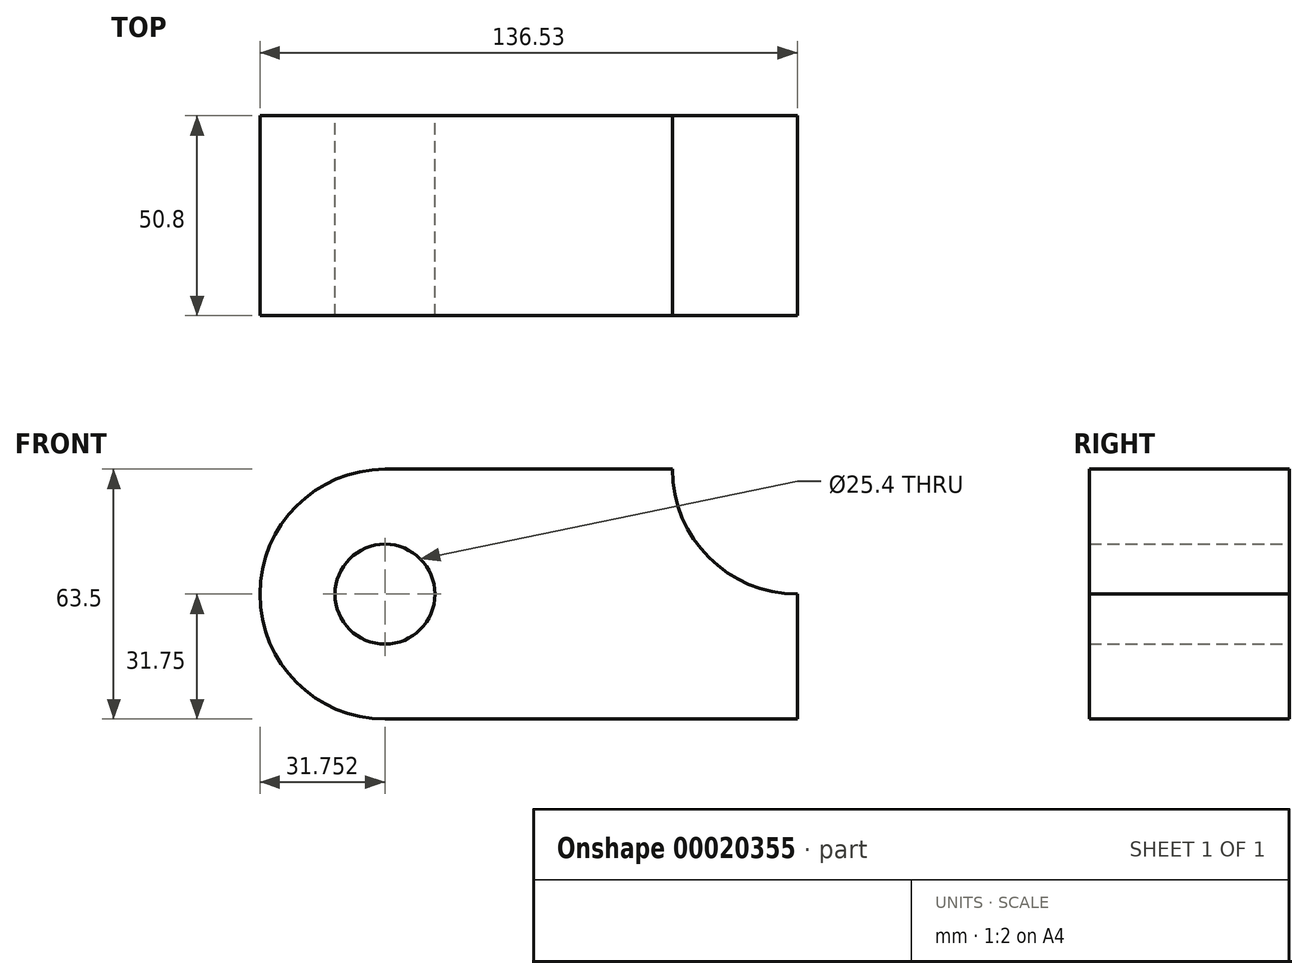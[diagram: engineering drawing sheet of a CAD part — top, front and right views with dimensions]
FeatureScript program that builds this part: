
annotation { "Feature Type Name" : "Feature", "Feature Type Description" : "" }
export const myFeature = defineFeature(function(context is Context, id is Id, definition is map)
    precondition{}
    {
        {
            var Q0;
            Q0=qCreatedBy(makeId("Front.planeOp"),FACE);
            var sketch = newSketch(context, id + "F0", { "sketchPlane" : qUnion([Q0])});
            skLineSegment(sketch, "E0.rect.bottom", {"start": v(-52.39, 31.75) * mm, "end": v(52.39, 31.75) * mm});
            skLineSegment(sketch, "E0.rect.top", {"start": v(-52.39, -31.75) * mm, "end": v(52.39, -31.75) * mm});
            skLineSegment(sketch, "E0.rect.left", {"start": v(-52.39, 31.75) * mm, "end": v(-52.39, -31.75) * mm});
            skLineSegment(sketch, "E0.rect.right", {"start": v(52.39, 31.75) * mm, "end": v(52.39, -31.75) * mm});
            skPoint(sketch, "E0.rect.middle", {"position": v(0, 0) * mm});
            skCircle(sketch, "E1", {"center": v(52.39, 31.75) * mm, "radius": 31.75 * mm});
            skCircle(sketch, "E2", {"center": v(-52.39, 0) * mm, "radius": 12.7 * mm});
            skCircle(sketch, "E3", {"center": v(-52.39, 0) * mm, "radius": 31.75 * mm});
            skSolve(sketch);
        }
        {
            var Q0;
            {var subQ1=sQuery(id+"F0.wireOp",EDGE,"E0.rect.top");Q0=makeQuery(id+"F0.imprint","IMPRINT",FACE,{"disambiguationData":[TD([[makeQuery(id+"F0.imprint","IMPRINT",EDGE,{"derivedFrom":subQ1}),1.0]])]});}
            var Q1;
            {var subQ1=sQuery(id+"F0.wireOp",EDGE,"E0.rect.left");var subQ4=sQuery(id+"F0.wireOp",EDGE,"E2");var subQ6=makeQuery(id+"F0.imprint","INTERSECT",VERTEX,{"disambiguationData":[OD(0.0)],"derivedFrom":[subQ1,subQ4]});Q1=makeQuery(id+"F0.imprint","IMPRINT",FACE,{"disambiguationData":[TD([[makeQuery(id+"F0.imprint","IMPRINT",EDGE,{"disambiguationData":[TD([[subQ6,1.0]])],"derivedFrom":subQ4}),-1.0]])]});}
            var Q2;
            {var subQ0=sQuery(id+"F0.wireOp",EDGE,"E2");var subQ1=sQuery(id+"F0.wireOp",EDGE,"E0.rect.left");var subQ3=makeQuery(id+"F0.imprint","INTERSECT",VERTEX,{"disambiguationData":[OD(0.0)],"derivedFrom":[subQ1,subQ0]});Q2=makeQuery(id+"F0.imprint","IMPRINT",FACE,{"disambiguationData":[TD([[makeQuery(id+"F0.imprint","IMPRINT",EDGE,{"disambiguationData":[TD([[subQ3,-1.0]])],"derivedFrom":subQ0}),-1.0]])]});}
            extrude(context, id + "F1", {"entities" : qUnion([Q0, Q1, Q2]), "depth" : 50.8 * mm});
        }
    });
